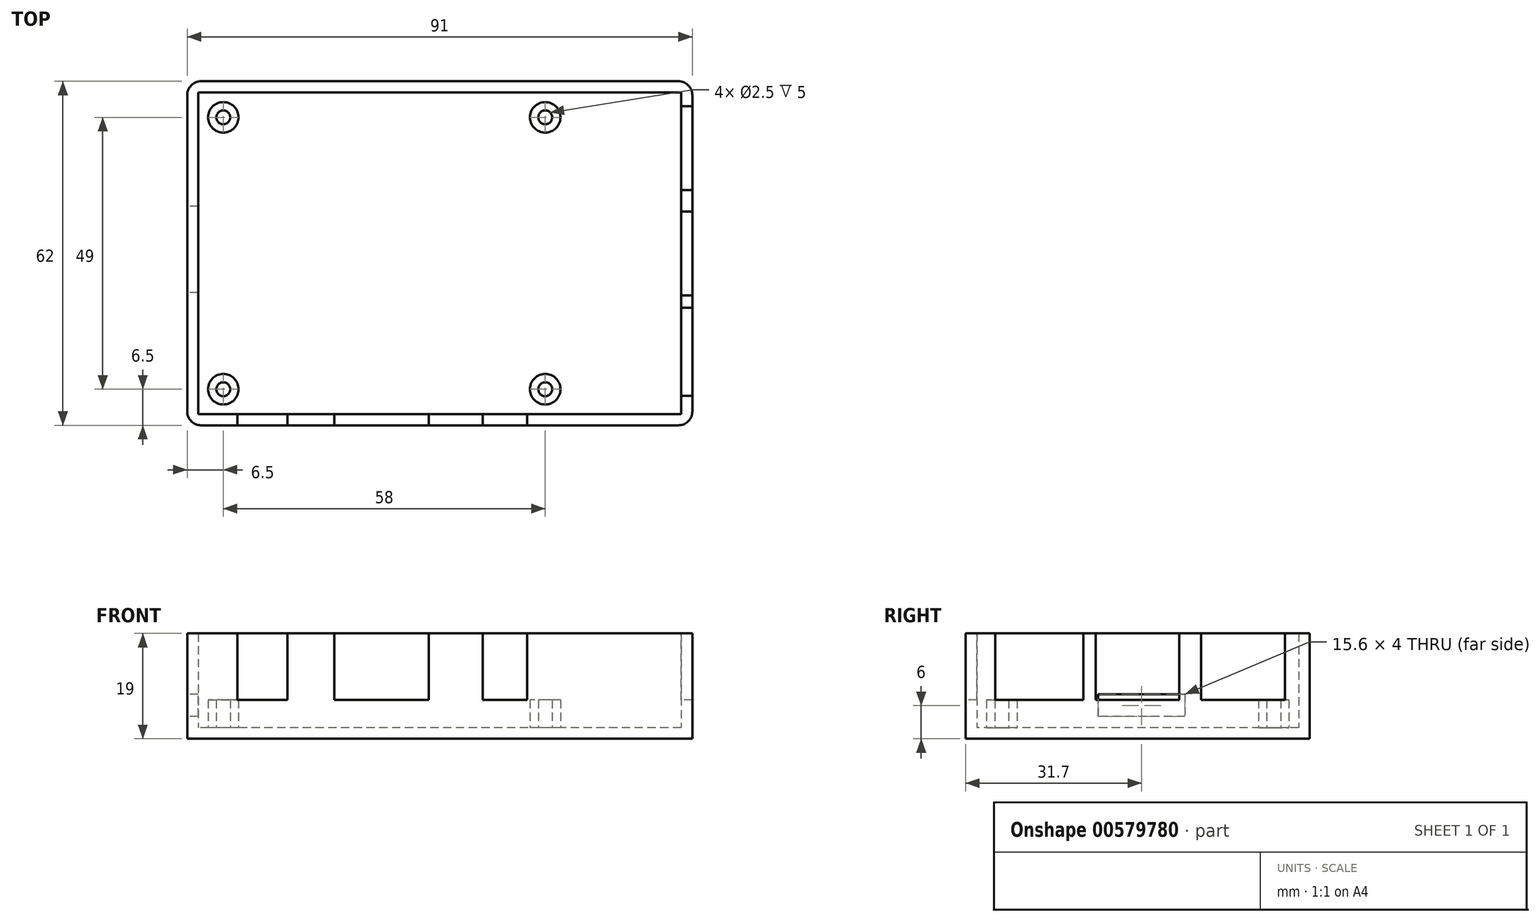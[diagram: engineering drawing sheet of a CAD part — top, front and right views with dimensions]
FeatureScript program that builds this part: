
annotation { "Feature Type Name" : "Feature", "Feature Type Description" : "" }
export const myFeature = defineFeature(function(context is Context, id is Id, definition is map)
    precondition{}
    {
        {
            var Q0;
            Q0=qCreatedBy(makeId("Top.planeOp"),FACE);
            var sketch = newSketch(context, id + "F0", { "sketchPlane" : qUnion([Q0])});
            skLineSegment(sketch, "E0.bottom", {"start": v(2.5, 0) * mm, "end": v(88.5, 0) * mm});
            skLineSegment(sketch, "E0.top", {"start": v(2.5, 62) * mm, "end": v(88.5, 62) * mm});
            skLineSegment(sketch, "E0.left", {"start": v(0, 2.5) * mm, "end": v(0, 59.5) * mm});
            skLineSegment(sketch, "E0.right", {"start": v(91, 2.5) * mm, "end": v(91, 59.5) * mm});
            skPoint(sketch, "E1.visualSharp", {"position": v(0, 62) * mm});
            skArc(sketch, "E1.filletArc", {"start": v(2.5, 62) * mm, "mid": v(0.73, 61.27) * mm, "end": v(0, 59.5) * mm});
            skPoint(sketch, "E2.visualSharp", {"position": v(91, 62) * mm});
            skArc(sketch, "E2.filletArc", {"start": v(91, 59.5) * mm, "mid": v(90.27, 61.27) * mm, "end": v(88.5, 62) * mm});
            skPoint(sketch, "E3.visualSharp", {"position": v(91, 0) * mm});
            skArc(sketch, "E3.filletArc", {"start": v(88.5, 0) * mm, "mid": v(90.27, 0.73) * mm, "end": v(91, 2.5) * mm});
            skPoint(sketch, "E4.visualSharp", {"position": v(0, 0) * mm});
            skArc(sketch, "E4.filletArc", {"start": v(0, 2.5) * mm, "mid": v(0.73, 0.73) * mm, "end": v(2.5, 0) * mm});
            skLineSegment(sketch, "E5.0", {"start": v(2, 60) * mm, "end": v(89, 60) * mm});
            skLineSegment(sketch, "E5.1", {"start": v(2, 2) * mm, "end": v(2, 60) * mm});
            skLineSegment(sketch, "E5.2", {"start": v(2, 2) * mm, "end": v(89, 2) * mm});
            skLineSegment(sketch, "E5.3", {"start": v(89, 2) * mm, "end": v(89, 60) * mm});
            skSolve(sketch);
        }
        {
            var Q0;
            Q0=makeQuery(id+"F0.imprint","IMPRINT",FACE,{"disambiguationData":[TD([[makeQuery(id+"F0.imprint","IMPRINT",EDGE,{"derivedFrom":sQuery(id+"F0.wireOp",EDGE,"E5.0")}),-1.0]])]});
            var Q1;
            Q1=makeQuery(id+"F0.imprint","IMPRINT",FACE,{"disambiguationData":[TD([[makeQuery(id+"F0.imprint","IMPRINT",EDGE,{"derivedFrom":sQuery(id+"F0.wireOp",EDGE,"E0.bottom")}),1.0]])]});
            extrude(context, id + "F1", {"entities" : qUnion([Q0, Q1]), "depth" : 2 * mm, "offsetDistance" : 25 * mm});
        }
        {
            var Q0;
            Q0 = qSketchRegion(id + "F0", true);
            extrude(context, id + "F2", {"entities" : qUnion([Q0]), "operationType" : NewBodyOperationType.ADD, "depth" : 19 * mm, "offsetDistance" : 25 * mm});
        }
        {
            var Q0;
            Q0=makeQuery(id+"F1.opExtrude","CAP_FACE",FACE,{"disambiguationData":[OSD([sQuery(id+"F0.wireOp",EDGE,"E0.bottom"),sQuery(id+"F0.wireOp",EDGE,"E0.top"),sQuery(id+"F0.wireOp",EDGE,"E0.left"),sQuery(id+"F0.wireOp",EDGE,"E0.right"),sQuery(id+"F0.wireOp",EDGE,"E1.filletArc"),sQuery(id+"F0.wireOp",EDGE,"E2.filletArc"),sQuery(id+"F0.wireOp",EDGE,"E3.filletArc"),sQuery(id+"F0.wireOp",EDGE,"E4.filletArc")])],"isStart":false});
            var sketch = newSketch(context, id + "F3", { "sketchPlane" : qUnion([Q0])});
            skCircle(sketch, "E6", {"center": v(6.5, 55.5) * mm, "radius": 2.75 * mm});
            skCircle(sketch, "E7", {"center": v(6.5, 6.5) * mm, "radius": 2.75 * mm});
            skCircle(sketch, "E8", {"center": v(64.5, 6.5) * mm, "radius": 2.75 * mm});
            skCircle(sketch, "E9", {"center": v(64.5, 55.5) * mm, "radius": 2.75 * mm});
            skCircle(sketch, "E10", {"center": v(6.5, 55.5) * mm, "radius": 1.25 * mm});
            skCircle(sketch, "E11", {"center": v(6.5, 6.5) * mm, "radius": 1.25 * mm});
            skCircle(sketch, "E12", {"center": v(64.5, 6.5) * mm, "radius": 1.25 * mm});
            skCircle(sketch, "E13", {"center": v(64.5, 55.5) * mm, "radius": 1.25 * mm});
            skSolve(sketch);
        }
        {
            var Q0;
            Q0 = qSketchRegion(id + "F3", true);
            extrude(context, id + "F4", {"entities" : qUnion([Q0]), "operationType" : NewBodyOperationType.ADD, "depth" : 5 * mm, "offsetDistance" : 25 * mm});
        }
        {
            var Q0;
            Q0=makeQuery(id+"F2.opExtrude","CAP_FACE",FACE,{"disambiguationData":[OSD([sQuery(id+"F0.wireOp",EDGE,"E0.bottom"),sQuery(id+"F0.wireOp",EDGE,"E0.top"),sQuery(id+"F0.wireOp",EDGE,"E0.left"),sQuery(id+"F0.wireOp",EDGE,"E0.right"),sQuery(id+"F0.wireOp",EDGE,"E1.filletArc"),sQuery(id+"F0.wireOp",EDGE,"E2.filletArc"),sQuery(id+"F0.wireOp",EDGE,"E3.filletArc"),sQuery(id+"F0.wireOp",EDGE,"E4.filletArc"),sQuery(id+"F0.wireOp",EDGE,"E5.0"),sQuery(id+"F0.wireOp",EDGE,"E5.1"),sQuery(id+"F0.wireOp",EDGE,"E5.2"),sQuery(id+"F0.wireOp",EDGE,"E5.3")])],"isStart":false});
            var sketch = newSketch(context, id + "F5", { "sketchPlane" : qUnion([Q0])});
            skLineSegment(sketch, "E14.bottom", {"start": v(9.05, 2) * mm, "end": v(18.05, 2) * mm});
            skLineSegment(sketch, "E14.top", {"start": v(9.05, 0) * mm, "end": v(18.05, 0) * mm});
            skLineSegment(sketch, "E14.left", {"start": v(9.05, 2) * mm, "end": v(9.05, 0) * mm});
            skLineSegment(sketch, "E14.right", {"start": v(18.05, 2) * mm, "end": v(18.05, 0) * mm});
            skLineSegment(sketch, "E15.bottom", {"start": v(26.5, 2) * mm, "end": v(43.5, 2) * mm});
            skLineSegment(sketch, "E15.top", {"start": v(26.5, 0) * mm, "end": v(43.5, 0) * mm});
            skLineSegment(sketch, "E15.left", {"start": v(26.5, 2) * mm, "end": v(26.5, 0) * mm});
            skLineSegment(sketch, "E15.right", {"start": v(43.5, 2) * mm, "end": v(43.5, 0) * mm});
            skLineSegment(sketch, "E16.bottom", {"start": v(53.25, 2) * mm, "end": v(61.25, 2) * mm});
            skLineSegment(sketch, "E16.top", {"start": v(53.25, 0) * mm, "end": v(61.25, 0) * mm});
            skLineSegment(sketch, "E16.left", {"start": v(53.25, 2) * mm, "end": v(53.25, 0) * mm});
            skLineSegment(sketch, "E16.right", {"start": v(61.25, 2) * mm, "end": v(61.25, 0) * mm});
            skLineSegment(sketch, "E17.bottom", {"start": v(91, 5.3) * mm, "end": v(89, 5.3) * mm});
            skLineSegment(sketch, "E17.top", {"start": v(91, 21.2) * mm, "end": v(89, 21.2) * mm});
            skLineSegment(sketch, "E17.left", {"start": v(91, 5.3) * mm, "end": v(91, 21.2) * mm});
            skLineSegment(sketch, "E17.right", {"start": v(89, 5.3) * mm, "end": v(89, 21.2) * mm});
            skLineSegment(sketch, "E18.bottom", {"start": v(91, 23.4) * mm, "end": v(89, 23.4) * mm});
            skLineSegment(sketch, "E18.top", {"start": v(91, 38.5) * mm, "end": v(89, 38.5) * mm});
            skLineSegment(sketch, "E18.left", {"start": v(91, 23.4) * mm, "end": v(91, 38.5) * mm});
            skLineSegment(sketch, "E18.right", {"start": v(89, 23.4) * mm, "end": v(89, 38.5) * mm});
            skLineSegment(sketch, "E19.bottom", {"start": v(91, 42.4) * mm, "end": v(89, 42.4) * mm});
            skLineSegment(sketch, "E19.top", {"start": v(91, 57.5) * mm, "end": v(89, 57.5) * mm});
            skLineSegment(sketch, "E19.left", {"start": v(91, 42.4) * mm, "end": v(91, 57.5) * mm});
            skLineSegment(sketch, "E19.right", {"start": v(89, 42.4) * mm, "end": v(89, 57.5) * mm});
            skLineSegment(sketch, "E20.bottom", {"start": v(0, 39.5) * mm, "end": v(2, 39.5) * mm});
            skLineSegment(sketch, "E20.top", {"start": v(0, 23.9) * mm, "end": v(2, 23.9) * mm});
            skLineSegment(sketch, "E20.left", {"start": v(0, 39.5) * mm, "end": v(0, 23.9) * mm});
            skLineSegment(sketch, "E20.right", {"start": v(2, 39.5) * mm, "end": v(2, 23.9) * mm});
            skSolve(sketch);
        }
        {
            var Q0;
            Q0=makeQuery(id+"F5.imprint","IMPRINT",FACE,{"disambiguationData":[TD([[makeQuery(id+"F5.imprint","IMPRINT",EDGE,{"derivedFrom":sQuery(id+"F5.wireOp",EDGE,"E14.bottom")}),-1.0]])]});
            var Q1;
            Q1=makeQuery(id+"F5.imprint","IMPRINT",FACE,{"disambiguationData":[TD([[makeQuery(id+"F5.imprint","IMPRINT",EDGE,{"derivedFrom":sQuery(id+"F5.wireOp",EDGE,"E15.bottom")}),-1.0]])]});
            var Q2;
            Q2=makeQuery(id+"F5.imprint","IMPRINT",FACE,{"disambiguationData":[TD([[makeQuery(id+"F5.imprint","IMPRINT",EDGE,{"derivedFrom":sQuery(id+"F5.wireOp",EDGE,"E16.bottom")}),-1.0]])]});
            var Q3;
            Q3=makeQuery(id+"F5.imprint","IMPRINT",FACE,{"disambiguationData":[TD([[makeQuery(id+"F5.imprint","IMPRINT",EDGE,{"derivedFrom":sQuery(id+"F5.wireOp",EDGE,"E17.bottom")}),-1.0]])]});
            var Q4;
            Q4=makeQuery(id+"F5.imprint","IMPRINT",FACE,{"disambiguationData":[TD([[makeQuery(id+"F5.imprint","IMPRINT",EDGE,{"derivedFrom":sQuery(id+"F5.wireOp",EDGE,"E18.bottom")}),-1.0]])]});
            var Q5;
            Q5=makeQuery(id+"F5.imprint","IMPRINT",FACE,{"disambiguationData":[TD([[makeQuery(id+"F5.imprint","IMPRINT",EDGE,{"derivedFrom":sQuery(id+"F5.wireOp",EDGE,"E19.bottom")}),-1.0]])]});
            extrude(context, id + "F6", {"entities" : qUnion([Q0, Q1, Q2, Q3, Q4, Q5]), "operationType" : NewBodyOperationType.REMOVE, "oppositeDirection" : true, "depth" : 12 * mm, "offsetDistance" : 25 * mm});
        }
        {
            var Q0;
            {var subQ0=sQuery(id+"F0.wireOp",EDGE,"E0.left");Q0=makeQuery(id+"F2.boolean.opBoolean","MERGE",FACE,{"derivedFrom":[makeQuery(id+"F1.opExtrude","SWEPT_FACE",FACE,{"disambiguationData":[OSD([subQ0])]}),makeQuery(id+"F2.opExtrude","SWEPT_FACE",FACE,{"disambiguationData":[OSD([subQ0])]})]});}
            var sketch = newSketch(context, id + "F7", { "sketchPlane" : qUnion([Q0])});
            skLineSegment(sketch, "E21.bottom", {"start": v(-39.5, 8) * mm, "end": v(-23.9, 8) * mm});
            skLineSegment(sketch, "E21.top", {"start": v(-39.5, 4) * mm, "end": v(-23.9, 4) * mm});
            skLineSegment(sketch, "E21.left", {"start": v(-39.5, 8) * mm, "end": v(-39.5, 4) * mm});
            skLineSegment(sketch, "E21.right", {"start": v(-23.9, 8) * mm, "end": v(-23.9, 4) * mm});
            skSolve(sketch);
        }
        {
            var Q0;
            Q0=makeQuery(id+"F7.imprint","IMPRINT",FACE,{"disambiguationData":[TD([[makeQuery(id+"F7.imprint","IMPRINT",EDGE,{"derivedFrom":sQuery(id+"F7.wireOp",EDGE,"E21.bottom")}),-1.0]])]});
            extrude(context, id + "F8", {"entities" : qUnion([Q0]), "operationType" : NewBodyOperationType.REMOVE, "endBound" : BoundingType.UP_TO_NEXT, "oppositeDirection" : true, "depth" : 25 * mm, "offsetDistance" : 25 * mm});
        }
    });
